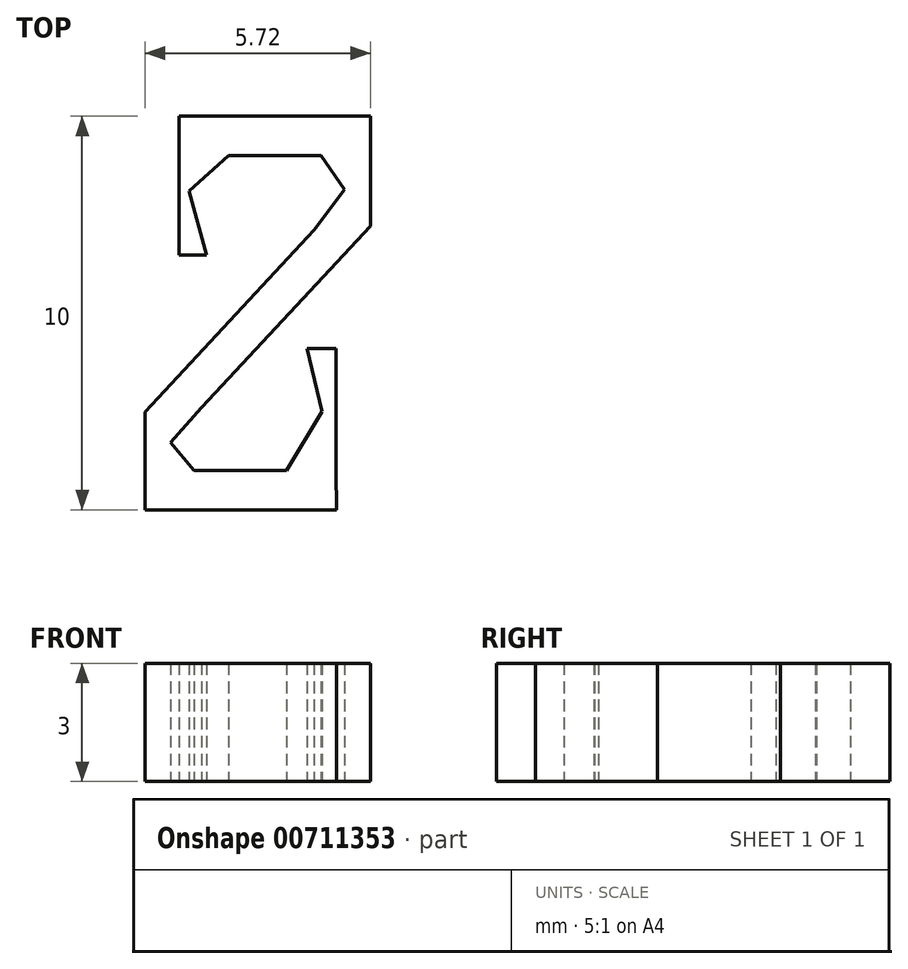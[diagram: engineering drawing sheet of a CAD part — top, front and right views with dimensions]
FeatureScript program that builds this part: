
annotation { "Feature Type Name" : "Feature", "Feature Type Description" : "" }
export const myFeature = defineFeature(function(context is Context, id is Id, definition is map)
    precondition{}
    {
        {
            var Q0;
            Q0=qCreatedBy(makeId("Top.planeOp"),FACE);
            var sketch = newSketch(context, id + "F0", { "sketchPlane" : qUnion([Q0])});
            skLineSegment(sketch, "E0", {"start": v(2.86, 2.21) * mm, "end": v(2.86, 4) * mm});
            skLineSegment(sketch, "E1", {"start": v(2.86, 4) * mm, "end": v(-2, 4) * mm});
            skLineSegment(sketch, "E2", {"start": v(-2, 4) * mm, "end": v(-2, 2.88) * mm});
            skLineSegment(sketch, "E3", {"start": v(-2, 2.88) * mm, "end": v(-0.74, 4) * mm});
            skLineSegment(sketch, "E4", {"start": v(1.6, 4) * mm, "end": v(2.86, 2.21) * mm});
            skLineSegment(sketch, "E5", {"start": v(-2.86, -2.52) * mm, "end": v(-2.86, -4) * mm});
            skLineSegment(sketch, "E6", {"start": v(-2.86, -4) * mm, "end": v(1.98, -4) * mm});
            skLineSegment(sketch, "E7", {"start": v(1.98, -4) * mm, "end": v(1.98, -1.93) * mm});
            skLineSegment(sketch, "E8", {"start": v(1.98, -1.93) * mm, "end": v(0.73, -4) * mm});
            skLineSegment(sketch, "E9", {"start": v(-1.62, -4) * mm, "end": v(-2.86, -2.52) * mm});
            skLineSegment(sketch, "E10", {"start": v(-2.86, -4) * mm, "end": v(-1.43, -2.4) * mm});
            skLineSegment(sketch, "E11.left", {"start": v(-2.86, -4) * mm, "end": v(-2.86, -4) * mm});
            skLineSegment(sketch, "E11.right", {"start": v(1.98, -4) * mm, "end": v(1.98, -4) * mm});
            skLineSegment(sketch, "E12.bottom", {"start": v(-2, 4) * mm, "end": v(2.86, 4) * mm});
            skLineSegment(sketch, "E12.top", {"start": v(-2, 5) * mm, "end": v(2.86, 5) * mm});
            skLineSegment(sketch, "E12.left", {"start": v(-2, 4) * mm, "end": v(-2, 5) * mm});
            skLineSegment(sketch, "E12.right", {"start": v(2.86, 4) * mm, "end": v(2.86, 5) * mm});
            skLineSegment(sketch, "E13", {"start": v(2.86, 4) * mm, "end": v(1.43, 2.1) * mm});
            skLineSegment(sketch, "E14", {"start": v(-2, 2.88) * mm, "end": v(-2, 1.47) * mm});
            skLineSegment(sketch, "E15", {"start": v(-2, 1.47) * mm, "end": v(-1.3, 1.47) * mm});
            skLineSegment(sketch, "E16", {"start": v(-1.3, 1.47) * mm, "end": v(-2, 4) * mm});
            skLineSegment(sketch, "E17", {"start": v(1.98, -1.93) * mm, "end": v(1.98, -0.9) * mm});
            skLineSegment(sketch, "E18", {"start": v(1.98, -0.9) * mm, "end": v(1.26, -0.9) * mm});
            skLineSegment(sketch, "E19", {"start": v(1.26, -0.9) * mm, "end": v(1.98, -4) * mm});
            skLineSegment(sketch, "E20", {"start": v(-1.43, -2.4) * mm, "end": v(2.86, 2.21) * mm});
            skLineSegment(sketch, "E21", {"start": v(-2.86, -2.52) * mm, "end": v(1.43, 2.1) * mm});
            skLineSegment(sketch, "E22", {"start": v(-2.86, -4) * mm, "end": v(-2.86, -5) * mm});
            skLineSegment(sketch, "E23", {"start": v(-2.86, -5) * mm, "end": v(2, -5) * mm});
            skLineSegment(sketch, "E24", {"start": v(2, -5) * mm, "end": v(1.98, -4) * mm});
            skSolve(sketch);
        }
        {
            var Q0;
            {var subQ4=sQuery(id+"F0.wireOp",EDGE,"E20");Q0=makeQuery(id+"F0.imprint","IMPRINT",FACE,{"disambiguationData":[TD([[makeQuery(id+"F0.imprint","IMPRINT",EDGE,{"derivedFrom":subQ4}),1.0]])]});}
            var Q1;
            {var subQ0=sQuery(id+"F0.wireOp",EDGE,"E5");Q1=makeQuery(id+"F0.imprint","IMPRINT",FACE,{"disambiguationData":[TD([[makeQuery(id+"F0.imprint","IMPRINT",EDGE,{"derivedFrom":subQ0}),1.0]])]});}
            var Q2;
            {var subQ3=sQuery(id+"F0.wireOp",EDGE,"E22");Q2=makeQuery(id+"F0.imprint","IMPRINT",FACE,{"disambiguationData":[TD([[makeQuery(id+"F0.imprint","IMPRINT",EDGE,{"derivedFrom":subQ3}),1.0]])]});}
            var Q3;
            {var subQ0=sQuery(id+"F0.wireOp",EDGE,"E7");Q3=makeQuery(id+"F0.imprint","IMPRINT",FACE,{"disambiguationData":[TD([[makeQuery(id+"F0.imprint","IMPRINT",EDGE,{"derivedFrom":subQ0}),1.0]])]});}
            var Q4;
            {var subQ0=sQuery(id+"F0.wireOp",EDGE,"E6");var subQ1=sQuery(id+"F0.wireOp",EDGE,"E8");var subQ2=makeQuery(id+"F0.imprint","INTERSECT",VERTEX,{"derivedFrom":[subQ1,subQ0]});Q4=makeQuery(id+"F0.imprint","IMPRINT",FACE,{"disambiguationData":[TD([[makeQuery(id+"F0.imprint","IMPRINT",EDGE,{"disambiguationData":[TD([[subQ2,1.0]])],"derivedFrom":subQ1}),1.0]])]});}
            var Q5;
            Q5=makeQuery(id+"F0.imprint","IMPRINT",FACE,{"disambiguationData":[TD([[makeQuery(id+"F0.imprint","IMPRINT",EDGE,{"derivedFrom":sQuery(id+"F0.wireOp",EDGE,"E12.top")}),-1.0]])]});
            var Q6;
            {var subQ0=sQuery(id+"F0.wireOp",EDGE,"E2");Q6=makeQuery(id+"F0.imprint","IMPRINT",FACE,{"disambiguationData":[TD([[makeQuery(id+"F0.imprint","IMPRINT",EDGE,{"derivedFrom":subQ0}),1.0]])]});}
            var Q7;
            {var subQ0=sQuery(id+"F0.wireOp",EDGE,"E14");Q7=makeQuery(id+"F0.imprint","IMPRINT",FACE,{"disambiguationData":[TD([[makeQuery(id+"F0.imprint","IMPRINT",EDGE,{"derivedFrom":subQ0}),1.0]])]});}
            var Q8;
            {var subQ0=sQuery(id+"F0.wireOp",EDGE,"E12.bottom");var subQ1=sQuery(id+"F0.wireOp",EDGE,"E3");var subQ2=makeQuery(id+"F0.imprint","INTERSECT",VERTEX,{"derivedFrom":[subQ1,subQ0]});Q8=makeQuery(id+"F0.imprint","IMPRINT",FACE,{"disambiguationData":[TD([[makeQuery(id+"F0.imprint","IMPRINT",EDGE,{"disambiguationData":[TD([[subQ2,1.0]])],"derivedFrom":subQ1}),1.0]])]});}
            var Q9;
            {var subQ0=sQuery(id+"F0.wireOp",EDGE,"E17");Q9=makeQuery(id+"F0.imprint","IMPRINT",FACE,{"disambiguationData":[TD([[makeQuery(id+"F0.imprint","IMPRINT",EDGE,{"derivedFrom":subQ0}),1.0]])]});}
            var Q10;
            {var subQ0=sQuery(id+"F0.wireOp",EDGE,"E0");Q10=makeQuery(id+"F0.imprint","IMPRINT",FACE,{"disambiguationData":[TD([[makeQuery(id+"F0.imprint","IMPRINT",EDGE,{"derivedFrom":subQ0}),1.0]])]});}
            var Q11;
            {var subQ0=sQuery(id+"F0.wireOp",EDGE,"E6");var subQ1=sQuery(id+"F0.wireOp",EDGE,"E9");var subQ2=makeQuery(id+"F0.imprint","INTERSECT",VERTEX,{"derivedFrom":[subQ1,subQ0]});Q11=makeQuery(id+"F0.imprint","IMPRINT",FACE,{"disambiguationData":[TD([[makeQuery(id+"F0.imprint","IMPRINT",EDGE,{"disambiguationData":[TD([[subQ2,-1.0]])],"derivedFrom":subQ1}),1.0]])]});}
            var Q12;
            {var subQ0=sQuery(id+"F0.wireOp",EDGE,"E12.bottom");var subQ1=sQuery(id+"F0.wireOp",EDGE,"E4");var subQ2=makeQuery(id+"F0.imprint","INTERSECT",VERTEX,{"derivedFrom":[subQ1,subQ0]});Q12=makeQuery(id+"F0.imprint","IMPRINT",FACE,{"disambiguationData":[TD([[makeQuery(id+"F0.imprint","IMPRINT",EDGE,{"disambiguationData":[TD([[subQ2,-1.0]])],"derivedFrom":subQ1}),1.0]])]});}
            var Q13;
            Q13=sQuery(id+"F0.wireOp",EDGE,"E13");
            var Q14;
            Q14=sQuery(id+"F0.wireOp",EDGE,"E18");
            var Q15;
            Q15=sQuery(id+"F0.wireOp",EDGE,"E17");
            var Q16;
            Q16=sQuery(id+"F0.wireOp",EDGE,"E3");
            var Q17;
            Q17=sQuery(id+"F0.wireOp",EDGE,"E4");
            var Q18;
            Q18=sQuery(id+"F0.wireOp",EDGE,"E14");
            var Q19;
            Q19=sQuery(id+"F0.wireOp",EDGE,"E2");
            var Q20;
            Q20=sQuery(id+"F0.wireOp",EDGE,"E12.top");
            var Q21;
            Q21=sQuery(id+"F0.wireOp",EDGE,"E7");
            var Q22;
            Q22=sQuery(id+"F0.wireOp",EDGE,"E8");
            var Q23;
            Q23=sQuery(id+"F0.wireOp",EDGE,"E6");
            var Q24;
            Q24=sQuery(id+"F0.wireOp",EDGE,"E5");
            var Q25;
            Q25=sQuery(id+"F0.wireOp",EDGE,"E23");
            var Q26;
            Q26=sQuery(id+"F0.wireOp",EDGE,"E0");
            var Q27;
            Q27=sQuery(id+"F0.wireOp",EDGE,"E12.bottom");
            var Q28;
            Q28=sQuery(id+"F0.wireOp",EDGE,"E19");
            var Q29;
            Q29=sQuery(id+"F0.wireOp",EDGE,"E21");
            var Q30;
            Q30=sQuery(id+"F0.wireOp",EDGE,"E10");
            var Q31;
            Q31=sQuery(id+"F0.wireOp",EDGE,"E16");
            var Q32;
            Q32=sQuery(id+"F0.wireOp",EDGE,"E20");
            var Q33;
            Q33=sQuery(id+"F0.wireOp",EDGE,"E9");
            var Q34;
            Q34=sQuery(id+"F0.wireOp",EDGE,"E6");
            var Q35;
            Q35=sQuery(id+"F0.wireOp",EDGE,"E1");
            var Q36;
            Q36=sQuery(id+"F0.wireOp",EDGE,"E22");
            var Q37;
            Q37=sQuery(id+"F0.wireOp",EDGE,"E24");
            var Q38;
            Q38=sQuery(id+"F0.wireOp",EDGE,"E12.left");
            var Q39;
            Q39=sQuery(id+"F0.wireOp",EDGE,"E12.right");
            var Q40;
            Q40=sQuery(id+"F0.wireOp",EDGE,"E15");
            extrude(context, id + "F1", {"entities" : qUnion([Q0, Q1, Q2, Q3, Q4, Q5, Q6, Q7, Q8, Q9, Q10, Q11, Q12]), "surfaceEntities" : qUnion([Q13, Q14, Q15, Q16, Q17, Q18, Q19, Q20, Q21, Q22, Q23, Q24, Q25, Q26, Q27, Q28, Q29, Q30, Q31, Q32, Q33, Q34, Q35, Q36, Q37, Q38, Q39, Q40]), "depth" : 3 * mm, "offsetDistance" : 25 * mm});
        }
    });
